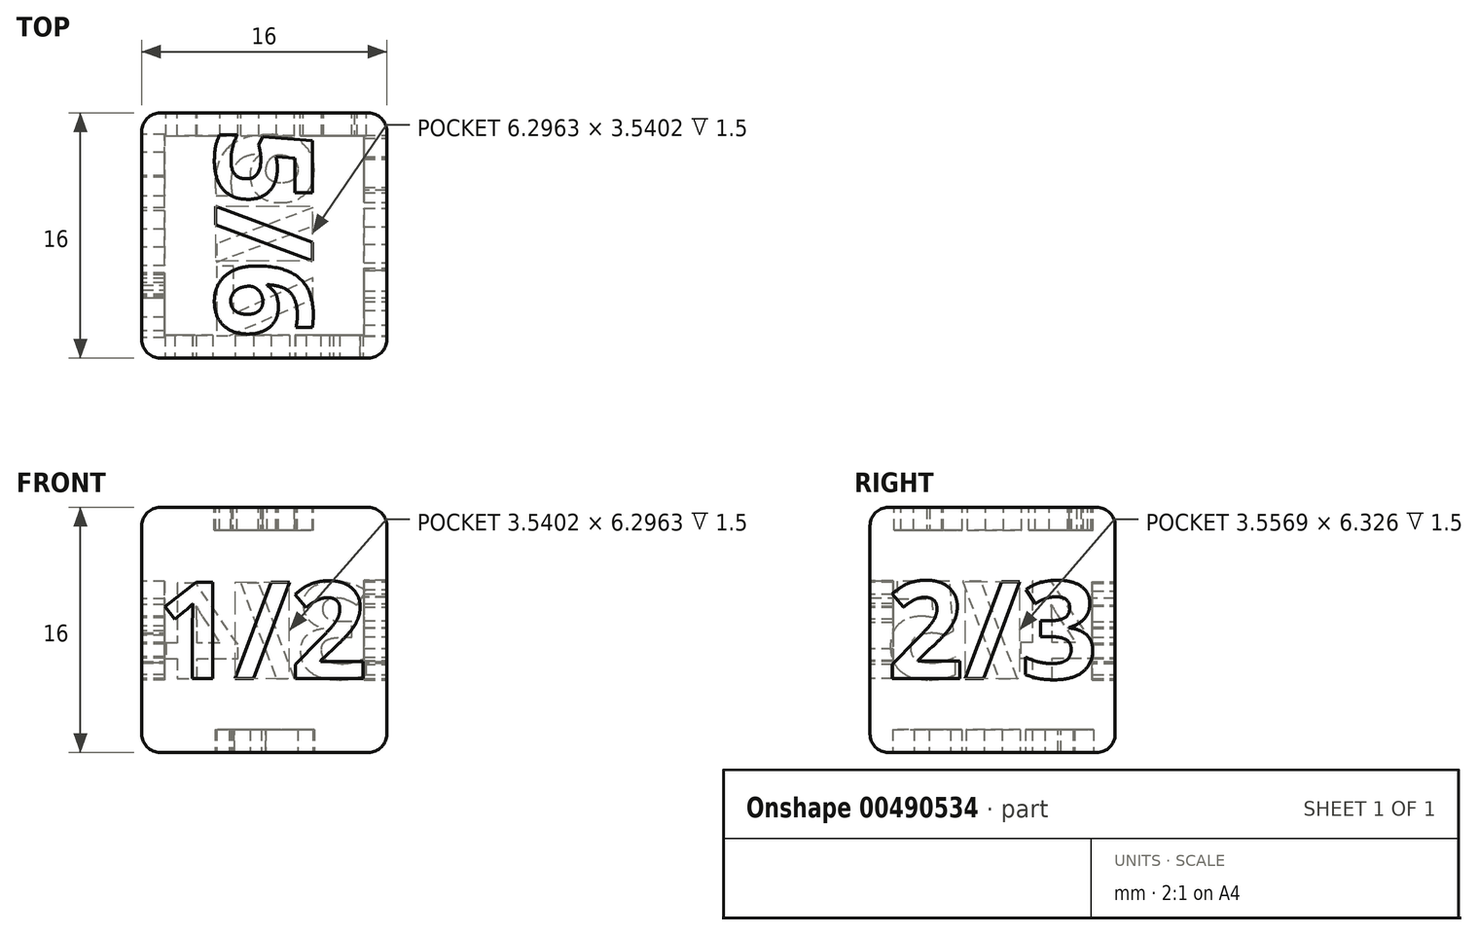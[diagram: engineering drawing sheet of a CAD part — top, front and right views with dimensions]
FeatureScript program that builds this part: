
annotation { "Feature Type Name" : "Feature", "Feature Type Description" : "" }
export const myFeature = defineFeature(function(context is Context, id is Id, definition is map)
    precondition{}
    {
        {
            var Q0;
            Q0=qCreatedBy(makeId("Top.planeOp"),FACE);
            var sketch = newSketch(context, id + "F0", { "sketchPlane" : qUnion([Q0])});
            skLineSegment(sketch, "E0.bottom", {"start": v(8, -8) * mm, "end": v(-8, -8) * mm});
            skLineSegment(sketch, "E0.top", {"start": v(8, 8) * mm, "end": v(-8, 8) * mm});
            skLineSegment(sketch, "E0.left", {"start": v(8, -8) * mm, "end": v(8, 8) * mm});
            skLineSegment(sketch, "E0.right", {"start": v(-8, -8) * mm, "end": v(-8, 8) * mm});
            skPoint(sketch, "E0.middle", {"position": v(0, 0) * mm});
            skSolve(sketch);
        }
        {
            var Q0;
            Q0=qCreatedBy(makeId("Top.planeOp"),FACE);
            var sketch = newSketch(context, id + "F1", { "sketchPlane" : qUnion([Q0])});
            skLineSegment(sketch, "E1.bottom", {"start": v(8, -8) * mm, "end": v(-8, -8) * mm});
            skLineSegment(sketch, "E1.top", {"start": v(8, 8) * mm, "end": v(-8, 8) * mm});
            skLineSegment(sketch, "E1.left", {"start": v(8, -8) * mm, "end": v(8, 8) * mm});
            skLineSegment(sketch, "E1.right", {"start": v(-8, -8) * mm, "end": v(-8, 8) * mm});
            skPoint(sketch, "E1.middle", {"position": v(0, 0) * mm});
            skSolve(sketch);
        }
        {
            var Q0;
            Q0 = qSketchRegion(id + "F0", true);
            extrude(context, id + "F2", {"entities" : qUnion([Q0]), "depth" : 8 * mm});
        }
        {
            var Q0;
            Q0 = qSketchRegion(id + "F1", true);
            extrude(context, id + "F3", {"entities" : qUnion([Q0]), "operationType" : NewBodyOperationType.ADD, "oppositeDirection" : true, "depth" : 8 * mm});
        }
        {
            var Q0;
            Q0=qCreatedBy(makeId("Front.planeOp"),FACE);
            cPlane(context, id + "F4", {"entities" : qUnion([Q0]), "cplaneType" : CPlaneType.OFFSET, "offset" : 8 * mm, "width" : 150 * mm, "height" : 150 * mm});
        }
        {
            var Q0;
            Q0=qCreatedBy(makeId("Right.planeOp"),FACE);
            cPlane(context, id + "F5", {"entities" : qUnion([Q0]), "cplaneType" : CPlaneType.OFFSET, "offset" : 8 * mm, "width" : 150 * mm, "height" : 150 * mm});
        }
        {
            var Q0;
            Q0=makeQuery(id+"F3.boolean.opBoolean","MERGE",FACE,{"derivedFrom":[makeQuery(id+"F2.opExtrude","SWEPT_FACE",FACE,{"disambiguationData":[OSD([sQuery(id+"F0.wireOp",EDGE,"E0.top")])]}),makeQuery(id+"F3.opExtrude","SWEPT_FACE",FACE,{"disambiguationData":[OSD([sQuery(id+"F1.wireOp",EDGE,"E1.top")])]})]});
            cPlane(context, id + "F6", {"entities" : qUnion([Q0]), "cplaneType" : CPlaneType.OFFSET, "offset" : 0 * mm, "width" : 150 * mm, "height" : 150 * mm});
        }
        {
            var Q0;
            Q0=makeQuery(id+"F3.boolean.opBoolean","MERGE",FACE,{"derivedFrom":[makeQuery(id+"F2.opExtrude","SWEPT_FACE",FACE,{"disambiguationData":[OSD([sQuery(id+"F0.wireOp",EDGE,"E0.right")])]}),makeQuery(id+"F3.opExtrude","SWEPT_FACE",FACE,{"disambiguationData":[OSD([sQuery(id+"F1.wireOp",EDGE,"E1.right")])]})]});
            cPlane(context, id + "F7", {"entities" : qUnion([Q0]), "cplaneType" : CPlaneType.OFFSET, "offset" : 0 * mm, "width" : 150 * mm, "height" : 150 * mm});
        }
        {
            var Q0;
            Q0=makeQuery(id+"F2.opExtrude","CAP_FACE",FACE,{"disambiguationData":[OSD([sQuery(id+"F0.wireOp",EDGE,"E0.bottom"),sQuery(id+"F0.wireOp",EDGE,"E0.top"),sQuery(id+"F0.wireOp",EDGE,"E0.left"),sQuery(id+"F0.wireOp",EDGE,"E0.right")])],"isStart":false});
            cPlane(context, id + "F8", {"entities" : qUnion([Q0]), "cplaneType" : CPlaneType.OFFSET, "offset" : 0 * mm, "width" : 150 * mm, "height" : 150 * mm});
        }
        {
            var Q0;
            Q0=makeQuery(id+"F3.opExtrude","CAP_FACE",FACE,{"disambiguationData":[OSD([sQuery(id+"F1.wireOp",EDGE,"E1.bottom"),sQuery(id+"F1.wireOp",EDGE,"E1.top"),sQuery(id+"F1.wireOp",EDGE,"E1.left"),sQuery(id+"F1.wireOp",EDGE,"E1.right")])],"isStart":false});
            cPlane(context, id + "F9", {"entities" : qUnion([Q0]), "cplaneType" : CPlaneType.OFFSET, "offset" : 0 * mm, "width" : 150 * mm, "height" : 150 * mm});
        }
        {
            var Q0;
            Q0=qCreatedBy(id+"F4.planeOp",FACE);
            var sketch = newSketch(context, id + "F10", { "sketchPlane" : qUnion([Q0])});
            skText(sketch, "E2", { "text": "1/2", "fontName": "OpenSans-Bold.ttf"});
            const initialGuessF10  = {"E2": [-0.007, -0.00317, 1, 0, 0.00635]};
            skSetInitialGuess(sketch, initialGuessF10);
            skSolve(sketch);
        }
        {
            var Q0;
            Q0=qCreatedBy(id+"F5.planeOp",FACE);
            var sketch = newSketch(context, id + "F11", { "sketchPlane" : qUnion([Q0])});
            skText(sketch, "E3", { "text": "2/3", "fontName": "OpenSans-Bold.ttf"});
            const initialGuessF11  = {"E3": [-0.0069, -0.00317, 1, 0, 0.00638]};
            skSetInitialGuess(sketch, initialGuessF11);
            skSolve(sketch);
        }
        {
            var Q0;
            Q0=qCreatedBy(id+"F6.planeOp",FACE);
            var sketch = newSketch(context, id + "F12", { "sketchPlane" : qUnion([Q0])});
            skText(sketch, "E4", { "text": "3/4", "fontName": "OpenSans-Bold.ttf"});
            const initialGuessF12  = {"E4": [-0.007, -0.00317, 1, 0, 0.00628]};
            skSetInitialGuess(sketch, initialGuessF12);
            skSolve(sketch);
        }
        {
            var Q0;
            Q0=qCreatedBy(id+"F7.planeOp",FACE);
            var sketch = newSketch(context, id + "F13", { "sketchPlane" : qUnion([Q0])});
            skText(sketch, "E5", { "text": "4/5", "fontName": "OpenSans-Bold.ttf"});
            const initialGuessF13  = {"E5": [-0.00675, -0.00317, 1, 0, 0.0064]};
            skSetInitialGuess(sketch, initialGuessF13);
            skSolve(sketch);
        }
        {
            var Q0;
            Q0=qCreatedBy(id+"F8.planeOp",FACE);
            var sketch = newSketch(context, id + "F14", { "sketchPlane" : qUnion([Q0])});
            skText(sketch, "E6", { "text": "5/6", "fontName": "OpenSans-Bold.ttf"});
            const initialGuessF14  = {"E6": [-0.00317, 0.007, 0, -1, 0.00635]};
            skSetInitialGuess(sketch, initialGuessF14);
            skSolve(sketch);
        }
        {
            var Q0;
            Q0=qCreatedBy(id+"F9.planeOp",FACE);
            var sketch = newSketch(context, id + "F15", { "sketchPlane" : qUnion([Q0])});
            skText(sketch, "E7", { "text": "6/7", "fontName": "OpenSans-Bold.ttf"});
            const initialGuessF15  = {"E7": [0.00317, -0.0069, 0, 1, 0.00635]};
            skSetInitialGuess(sketch, initialGuessF15);
            skSolve(sketch);
        }
        {
            var Q0;
            Q0=makeQuery(id+"F3.boolean.opBoolean","MERGE",FACE,{"derivedFrom":[makeQuery(id+"F2.opExtrude","SWEPT_FACE",FACE,{"disambiguationData":[OSD([sQuery(id+"F0.wireOp",EDGE,"E0.top")])]}),makeQuery(id+"F3.opExtrude","SWEPT_FACE",FACE,{"disambiguationData":[OSD([sQuery(id+"F1.wireOp",EDGE,"E1.top")])]})]});
            var Q1;
            Q1=makeQuery(id+"F3.boolean.opBoolean","MERGE",FACE,{"derivedFrom":[makeQuery(id+"F2.opExtrude","SWEPT_FACE",FACE,{"disambiguationData":[OSD([sQuery(id+"F0.wireOp",EDGE,"E0.bottom")])]}),makeQuery(id+"F3.opExtrude","SWEPT_FACE",FACE,{"disambiguationData":[OSD([sQuery(id+"F1.wireOp",EDGE,"E1.bottom")])]})]});
            var Q2;
            Q2=makeQuery(id+"F3.boolean.opBoolean","MERGE",FACE,{"derivedFrom":[makeQuery(id+"F2.opExtrude","SWEPT_FACE",FACE,{"disambiguationData":[OSD([sQuery(id+"F0.wireOp",EDGE,"E0.right")])]}),makeQuery(id+"F3.opExtrude","SWEPT_FACE",FACE,{"disambiguationData":[OSD([sQuery(id+"F1.wireOp",EDGE,"E1.right")])]})]});
            var Q3;
            Q3=makeQuery(id+"F3.boolean.opBoolean","MERGE",FACE,{"derivedFrom":[makeQuery(id+"F2.opExtrude","SWEPT_FACE",FACE,{"disambiguationData":[OSD([sQuery(id+"F0.wireOp",EDGE,"E0.left")])]}),makeQuery(id+"F3.opExtrude","SWEPT_FACE",FACE,{"disambiguationData":[OSD([sQuery(id+"F1.wireOp",EDGE,"E1.left")])]})]});
            fillet(context, id + "F16", {"entities" : qUnion([Q0, Q1, Q2, Q3]), "radius" : 1.2 * mm, "tangentPropagation" : true, "allowEdgeOverflow" : false});
        }
        {
            var Q0;
            Q0 = qSketchRegion(id + "F10", true);
            extrude(context, id + "F17", {"entities" : qUnion([Q0]), "operationType" : NewBodyOperationType.REMOVE, "oppositeDirection" : true, "depth" : 1.5 * mm});
        }
        {
            var Q0;
            Q0 = qSketchRegion(id + "F11", true);
            extrude(context, id + "F18", {"entities" : qUnion([Q0]), "operationType" : NewBodyOperationType.REMOVE, "oppositeDirection" : true, "depth" : 1.5 * mm});
        }
        {
            var Q0;
            Q0 = qSketchRegion(id + "F12", true);
            extrude(context, id + "F19", {"entities" : qUnion([Q0]), "operationType" : NewBodyOperationType.REMOVE, "oppositeDirection" : true, "depth" : 1.5 * mm});
        }
        {
            var Q0;
            Q0 = qSketchRegion(id + "F13", true);
            extrude(context, id + "F20", {"entities" : qUnion([Q0]), "operationType" : NewBodyOperationType.REMOVE, "oppositeDirection" : true, "depth" : 1.5 * mm});
        }
        {
            var Q0;
            Q0 = qSketchRegion(id + "F14", true);
            extrude(context, id + "F21", {"entities" : qUnion([Q0]), "operationType" : NewBodyOperationType.REMOVE, "oppositeDirection" : true, "depth" : 1.5 * mm});
        }
        {
            var Q0;
            Q0 = qSketchRegion(id + "F15", true);
            extrude(context, id + "F22", {"entities" : qUnion([Q0]), "operationType" : NewBodyOperationType.REMOVE, "oppositeDirection" : true, "depth" : 1.5 * mm});
        }
    });
